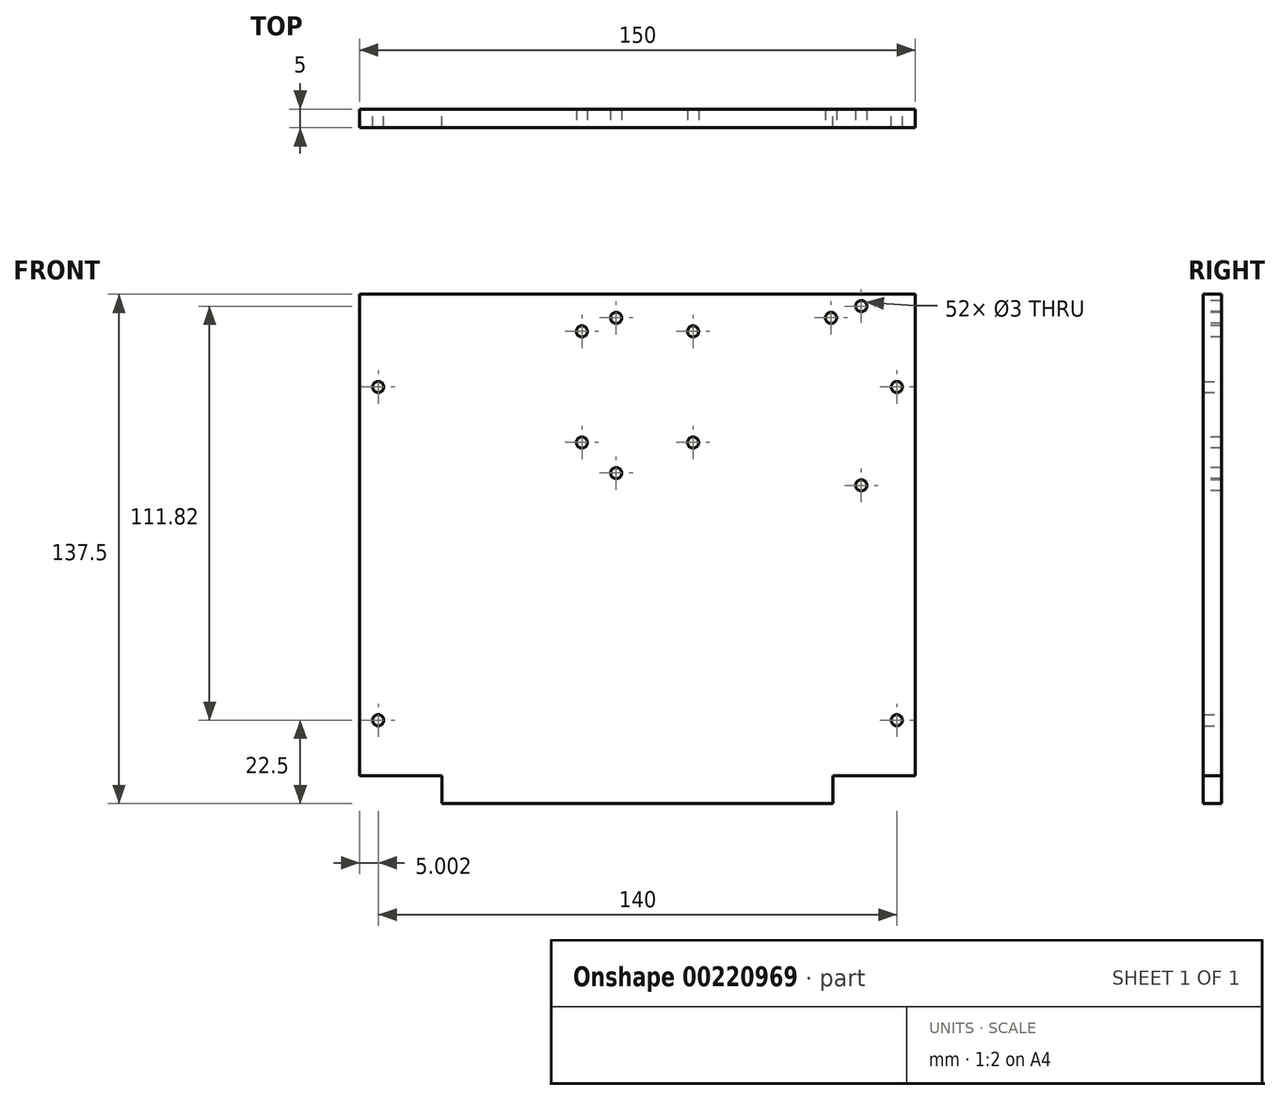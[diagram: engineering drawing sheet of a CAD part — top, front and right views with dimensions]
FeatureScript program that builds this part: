
annotation { "Feature Type Name" : "Feature", "Feature Type Description" : "" }
export const myFeature = defineFeature(function(context is Context, id is Id, definition is map)
    precondition{}
    {
        {
            var Q0;
            Q0=qCreatedBy(makeId("Front.planeOp"),FACE);
            var sketch = newSketch(context, id + "F0", { "sketchPlane" : qUnion([Q0])});
            skLineSegment(sketch, "E0.bottom", {"start": v(3.2, 0) * mm, "end": v(153.2, 0) * mm});
            skLineSegment(sketch, "E0.top", {"start": v(3.2, 130) * mm, "end": v(153.2, 130) * mm});
            skLineSegment(sketch, "E0.left", {"start": v(3.2, 0) * mm, "end": v(3.2, 130) * mm});
            skLineSegment(sketch, "E0.right", {"start": v(153.2, 0) * mm, "end": v(153.2, 130) * mm});
            skLineSegment(sketch, "E1", {"start": v(3.2, 0) * mm, "end": v(3.2, 15) * mm});
            skLineSegment(sketch, "E2", {"start": v(3.2, 15) * mm, "end": v(8.2, 15) * mm});
            skLineSegment(sketch, "E3", {"start": v(8.2, 15) * mm, "end": v(8.2, 105) * mm});
            skCircle(sketch, "E4", {"center": v(8.2, 105) * mm, "radius": 1.5 * mm});
            skCircle(sketch, "E5", {"center": v(8.2, 15) * mm, "radius": 1.5 * mm});
            skLineSegment(sketch, "E6", {"start": v(153.2, 0) * mm, "end": v(153.2, 15) * mm});
            skLineSegment(sketch, "E7", {"start": v(153.2, 15) * mm, "end": v(148.2, 15) * mm});
            skLineSegment(sketch, "E8", {"start": v(148.2, 15) * mm, "end": v(148.2, 105) * mm});
            skCircle(sketch, "E9", {"center": v(148.2, 105) * mm, "radius": 1.5 * mm});
            skCircle(sketch, "E10", {"center": v(148.2, 15) * mm, "radius": 1.5 * mm});
            skLineSegment(sketch, "E11", {"start": v(3.2, 0) * mm, "end": v(25.44, 0) * mm});
            skLineSegment(sketch, "E12", {"start": v(153.2, 0) * mm, "end": v(130.94, 0) * mm});
            skLineSegment(sketch, "E13", {"start": v(25.44, 0) * mm, "end": v(25.44, -7.5) * mm});
            skLineSegment(sketch, "E14", {"start": v(130.94, 0) * mm, "end": v(130.94, -7.5) * mm});
            skLineSegment(sketch, "E15", {"start": v(25.44, -7.5) * mm, "end": v(130.94, -7.5) * mm});
            skSolve(sketch);
        }
        {
            var Q0;
            Q0 = qSketchRegion(id + "F0", true);
            extrude(context, id + "F1", {"entities" : qUnion([Q0]), "depth" : 5 * mm, "offsetDistance" : 25 * mm});
        }
        {
            var Q0;
            Q0=makeQuery(id+"F1.opExtrude","CAP_FACE",FACE,{"disambiguationData":[OSD([sQuery(id+"F0.wireOp",EDGE,"E0.top"),sQuery(id+"F0.wireOp",EDGE,"E0.left"),sQuery(id+"F0.wireOp",EDGE,"E0.right"),sQuery(id+"F0.wireOp",EDGE,"E1"),sQuery(id+"F0.wireOp",EDGE,"E4"),sQuery(id+"F0.wireOp",EDGE,"E5"),sQuery(id+"F0.wireOp",EDGE,"E6"),sQuery(id+"F0.wireOp",EDGE,"E9"),sQuery(id+"F0.wireOp",EDGE,"E10"),sQuery(id+"F0.wireOp",EDGE,"E11"),sQuery(id+"F0.wireOp",EDGE,"E12"),sQuery(id+"F0.wireOp",EDGE,"E13"),sQuery(id+"F0.wireOp",EDGE,"E14"),sQuery(id+"F0.wireOp",EDGE,"E15")])],"isStart":false});
            var sketch = newSketch(context, id + "F2", { "sketchPlane" : qUnion([Q0])});
            skLineSegment(sketch, "E16", {"start": v(153.2, 130) * mm, "end": v(138.58, 130) * mm});
            skLineSegment(sketch, "E17", {"start": v(138.58, 130) * mm, "end": v(138.58, 126.82) * mm});
            skLineSegment(sketch, "E18", {"start": v(138.58, 126.82) * mm, "end": v(138.58, 78.43) * mm});
            skLineSegment(sketch, "E19", {"start": v(72.42, 130) * mm, "end": v(72.42, 123.65) * mm});
            skCircle(sketch, "E20", {"center": v(138.58, 78.43) * mm, "radius": 1.5 * mm});
            skCircle(sketch, "E21", {"center": v(138.58, 126.82) * mm, "radius": 1.5 * mm});
            skCircle(sketch, "E22", {"center": v(72.42, 123.65) * mm, "radius": 1.5 * mm});
            skCircle(sketch, "E23", {"center": v(72.42, 81.74) * mm, "radius": 1.5 * mm});
            skLineSegment(sketch, "E24", {"start": v(153.2, 130) * mm, "end": v(129.7, 130) * mm});
            skLineSegment(sketch, "E25", {"start": v(129.7, 130) * mm, "end": v(129.7, 116.5) * mm});
            skLineSegment(sketch, "E26", {"start": v(78.2, 130) * mm, "end": v(78.2, 105) * mm});
            skLineSegment(sketch, "E27", {"start": v(78.2, 105) * mm, "end": v(63.2, 105) * mm});
            skLineSegment(sketch, "E28", {"start": v(63.2, 105) * mm, "end": v(63.2, 120) * mm});
            skCircle(sketch, "E29", {"center": v(63.2, 120) * mm, "radius": 1.5 * mm});
            skCircle(sketch, "E30.1.0", {"center": v(63.2, 90) * mm, "radius": 1.5 * mm});
            skCircle(sketch, "E30.2.0", {"center": v(93.2, 90) * mm, "radius": 1.5 * mm});
            skCircle(sketch, "E30.3.0", {"center": v(93.2, 120) * mm, "radius": 1.5 * mm});
            skPoint(sketch, "E30.center", {"position": v(78.2, 105) * mm});
            skLineSegment(sketch, "E31", {"start": v(93.2, 120) * mm, "end": v(93.2, 130) * mm});
            skLineSegment(sketch, "E32", {"start": v(93.2, 90) * mm, "end": v(93.2, 120) * mm});
            skLineSegment(sketch, "E33", {"start": v(63.2, 90) * mm, "end": v(63.2, 105) * mm});
            skLineSegment(sketch, "E34", {"start": v(72.42, 81.74) * mm, "end": v(72.42, 105) * mm});
            skLineSegment(sketch, "E35", {"start": v(72.42, 123.65) * mm, "end": v(72.42, 74.65) * mm});
            skCircle(sketch, "E36", {"center": v(130.42, 123.65) * mm, "radius": 1.5 * mm});
            skLineSegment(sketch, "E37", {"start": v(32.04, 130) * mm, "end": v(32.04, 75) * mm});
            skLineSegment(sketch, "E38", {"start": v(153.2, 44.12) * mm, "end": v(71.2, 44.12) * mm});
            skSolve(sketch);
        }
        {
            var Q0;
            Q0 = qSketchRegion(id + "F2", true);
            extrude(context, id + "F3", {"entities" : qUnion([Q0]), "operationType" : NewBodyOperationType.REMOVE, "oppositeDirection" : true, "depth" : 25 * mm, "offsetDistance" : 25 * mm});
        }
    });
